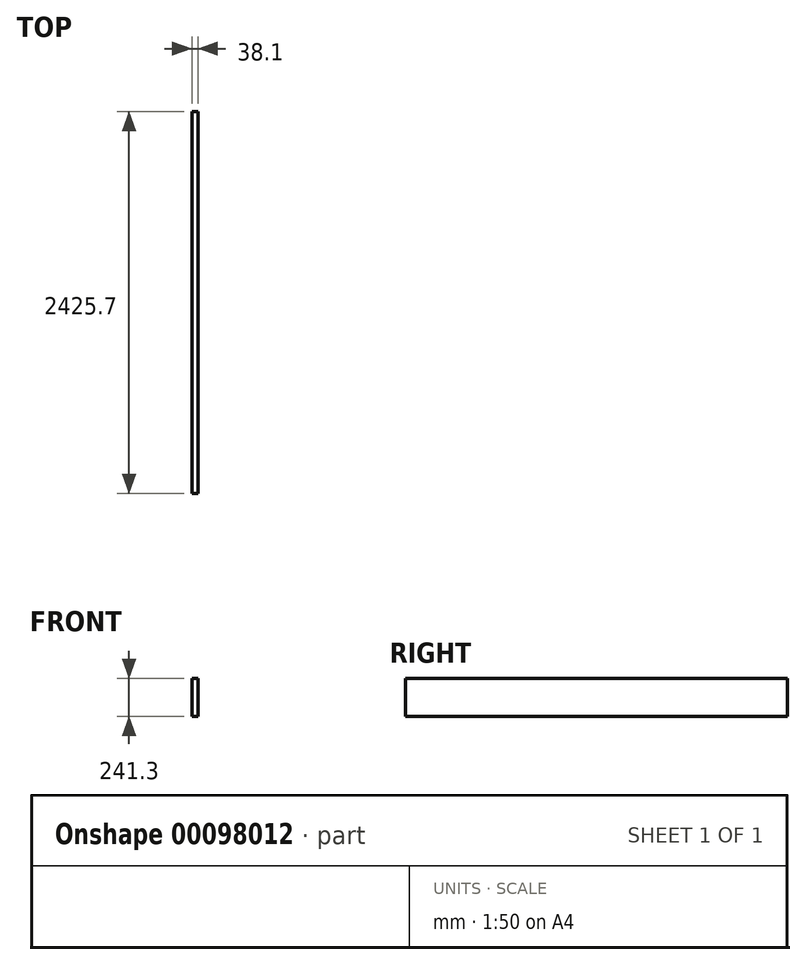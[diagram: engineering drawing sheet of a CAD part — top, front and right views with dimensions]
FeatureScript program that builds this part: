
annotation { "Feature Type Name" : "Feature", "Feature Type Description" : "" }
export const myFeature = defineFeature(function(context is Context, id is Id, definition is map)
    precondition{}
    {
        {
            var Q0;
            Q0=qCreatedBy(makeId("Right.planeOp"),FACE);
            var sketch = newSketch(context, id + "F0", { "sketchPlane" : qUnion([Q0])});
            skLineSegment(sketch, "E0.bottom", {"start": v(1212.85, 120.65) * mm, "end": v(-1212.85, 120.65) * mm});
            skLineSegment(sketch, "E0.top", {"start": v(1212.85, -120.65) * mm, "end": v(-1212.85, -120.65) * mm});
            skLineSegment(sketch, "E0.left", {"start": v(1212.85, 120.65) * mm, "end": v(1212.85, -120.65) * mm});
            skLineSegment(sketch, "E0.right", {"start": v(-1212.85, 120.65) * mm, "end": v(-1212.85, -120.65) * mm});
            skPoint(sketch, "E0.middle", {"position": v(0, 0) * mm});
            skSolve(sketch);
        }
        {
            var Q0;
            Q0=makeQuery(id+"F0.imprint","IMPRINT",FACE,{"disambiguationData":[TD([[makeQuery(id+"F0.imprint","IMPRINT",EDGE,{"derivedFrom":sQuery(id+"F0.wireOp",EDGE,"E0.bottom")}),1.0]])]});
            extrude(context, id + "F1", {"entities" : qUnion([Q0]), "depth" : 38.1 * mm});
        }
    });
